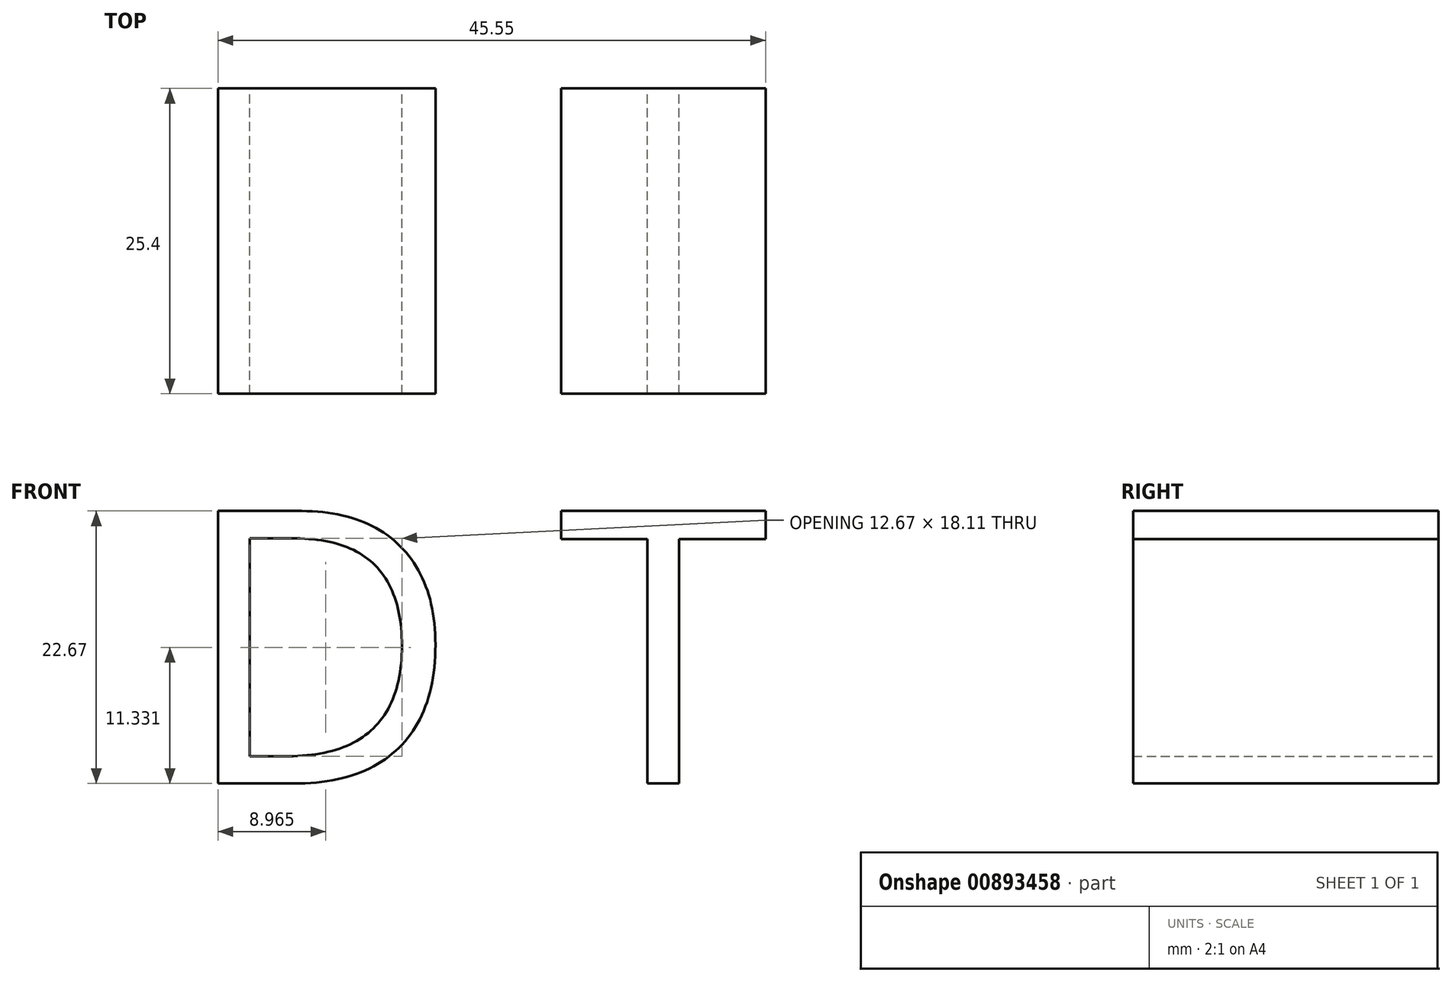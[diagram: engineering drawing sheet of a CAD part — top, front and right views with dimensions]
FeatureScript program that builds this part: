
annotation { "Feature Type Name" : "Feature", "Feature Type Description" : "" }
export const myFeature = defineFeature(function(context is Context, id is Id, definition is map)
    precondition{}
    {
        {
            var Q0;
            Q0=qCreatedBy(makeId("Front.planeOp"),FACE);
            var sketch = newSketch(context, id + "F0", { "sketchPlane" : qUnion([Q0])});
            skText(sketch, "E0", { "text": "D T", "fontName": "OpenSans-Regular.ttf"});
            const initialGuessF0  = {"E0": [-0.02548, -0.01294, 1, 0, 0.02286]};
            skSetInitialGuess(sketch, initialGuessF0);
            skSolve(sketch);
        }
        {
            var Q0;
            Q0 = qSketchRegion(id + "F0", true);
            extrude(context, id + "F1", {"entities" : qUnion([Q0]), "depth" : 25.4 * mm, "offsetDistance" : 25.4 * mm});
        }
    });
